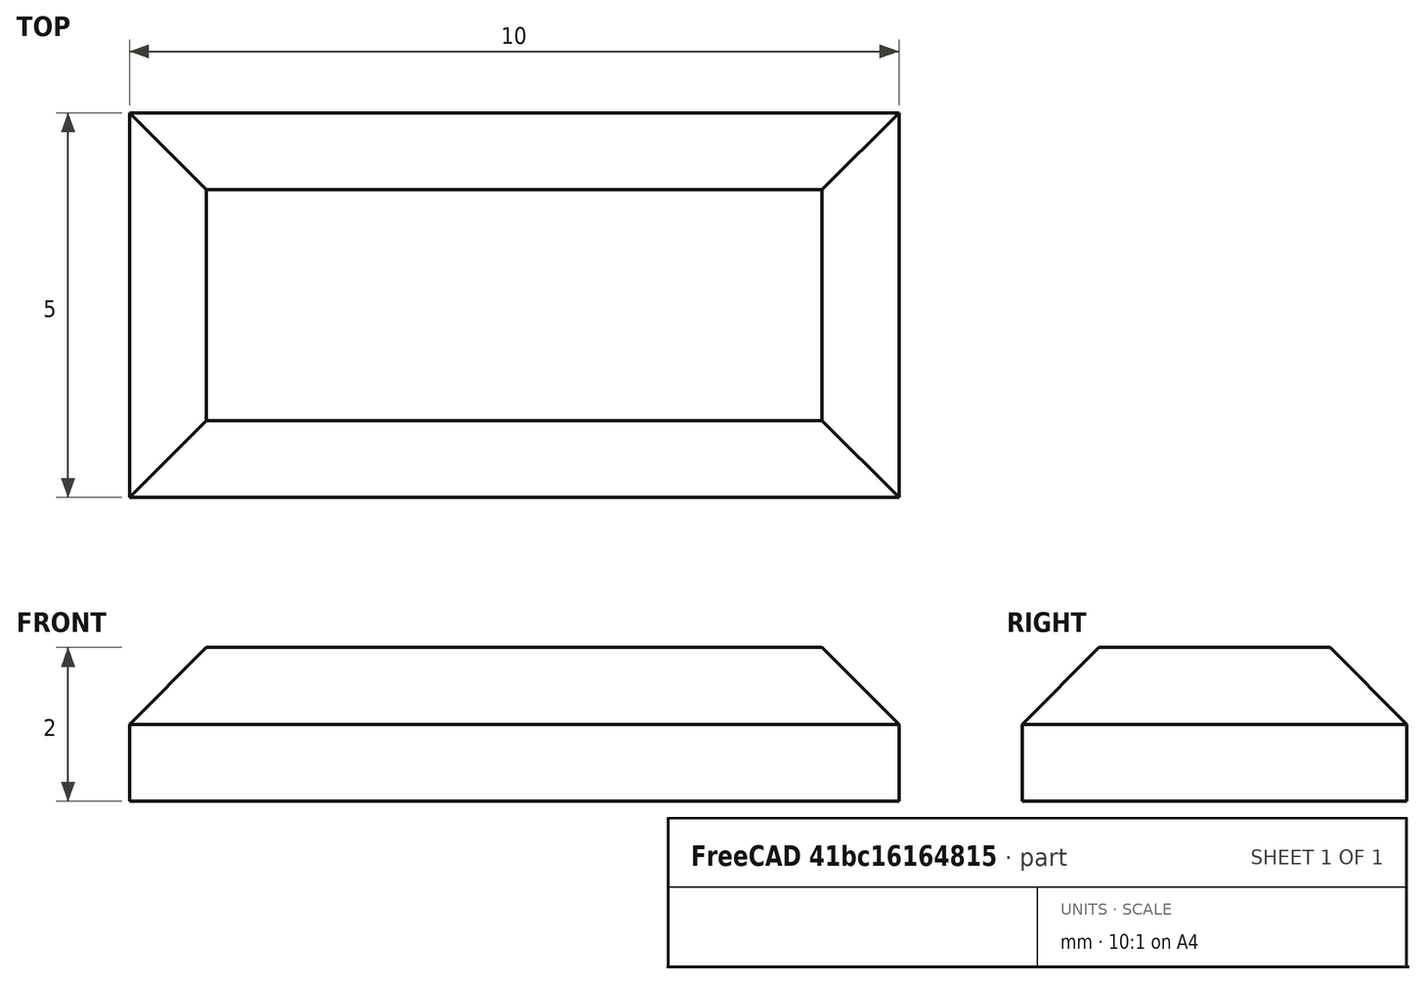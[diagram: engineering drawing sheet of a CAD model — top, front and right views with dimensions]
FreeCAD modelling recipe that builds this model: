
FCSTD DOCUMENT  (FreeCAD 0.21R33694 (Git))
Label: OJT1_T012R011_xocolata
License: All rights reserved
LicenseURL: http://en.wikipedia.org/wiki/All_rights_reserved
objects: Part::Box×1, Part::Chamfer×1, Part::FeaturePython×1
note: 2 computed .brp shape members not serialized (recipe doc carries the construction recipe); baked Part::Feature solids carry a one-line shape summary decoded from their .brp

FEATURE [Part::Box] Box  label="Cube"
  AttacherType = Attacher::AttachEngine3D
  Height = 2
  Length = 10
  Width = 5
FEATURE [Part::Chamfer] Chamfer
  Base = -> Box
  Edges = 4 edges r=1: [Edge2,Edge6,Edge10,Edge12]
FEATURE [Part::FeaturePython] Array  # Draft array (typed FeaturePython)
  AlwaysSyncPlacement = false
  Angle = 360
  ArrayType = 0
  Axis = (0,0,1)
  Base = -> Chamfer
  Center = (0,0,0)
  Count = 16
  ExpandArray = false
  Fuse = false
  IntervalAxis = (0,0,0)
  IntervalX = (10,0,0)
  IntervalY = (0,5,0)
  IntervalZ = (0,0,100)
  NumberCircles = 3
  NumberPolar = 5
  NumberX = 4
  NumberY = 4
  NumberZ = 1
  PlacementList = 16 placements: [(0,0,0),(0,5,0),(0,10,0),(0,15,0),(10,0,0),(10,5,0),(10,10,0),(10,15,0),(20,0,0),(20,5,0),(20,10,0),(20,15,0),(30,0,0),(30,5,0),(30,10,0),(30,15,0)]
  RadialDistance = 50
  ScaleList = (16) [(1,1,1),(1,1,1),(1,1,1),(1,1,1),(1,1,1),(1,1,1),(1,1,1),(1,1,1),(1,1,1),(1,1,1),(1,1,1),(1,1,1),(1,1,1),(1,1,1),(1,1,1),(1,1,1)]
  Symmetry = 1
  TangentialDistance = 25
